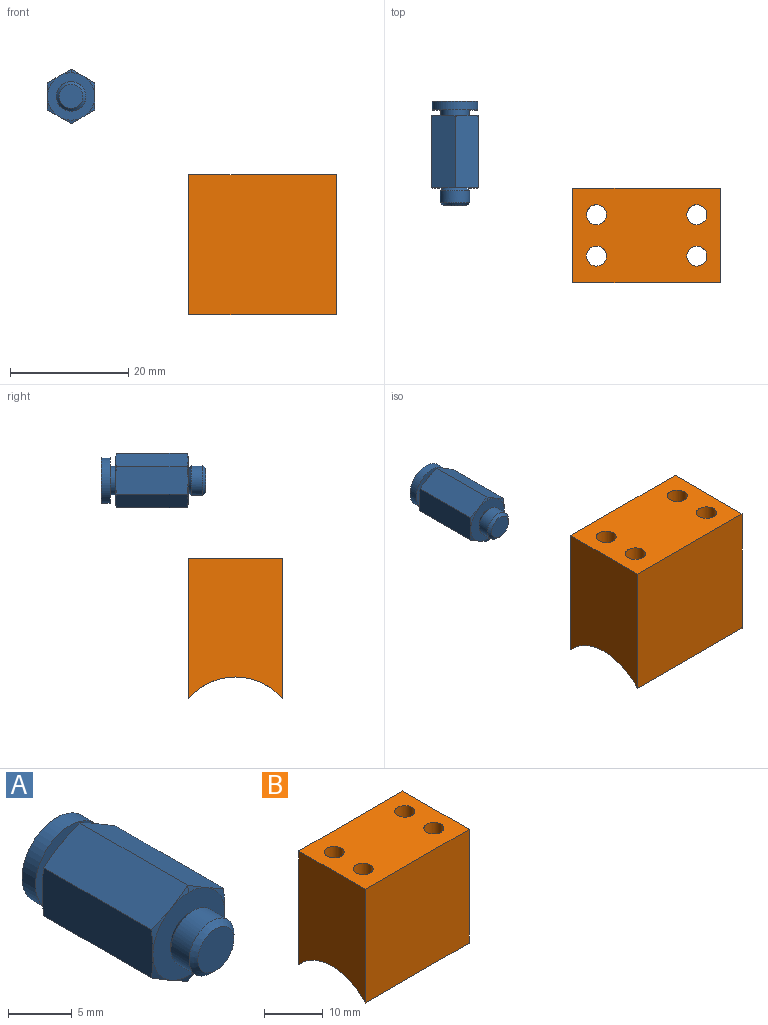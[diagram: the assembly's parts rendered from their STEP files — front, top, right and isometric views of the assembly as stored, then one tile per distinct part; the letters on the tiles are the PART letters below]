
ASSEMBLY  parts=2 mates=1
PART A: 32 faces, bbox 9.6x18x9.6 mm
  f0: plane 4x4mm, normal (0,1,0), area 12.6mm2, adj f1
  f1: cylinder r=2mm len=13.3mm, axis (0,-1,0), area 167.1mm2, adj f0,f2
  f2: plane 7.7x7.7mm, normal (0,1,0), area 34mm2, adj f1,f3
  f3: cylinder r=3.85mm len=7.7mm, axis (0,-1,0), area 36.3mm2, adj f2,f5
  f4: plane 4.02x4.02mm, normal (0,-1,0), area 12.7mm2, adj f6
  f5: plane 7.7x7.7mm, normal (0,-1,0), area 28.5mm2, adj f3,f10
  f6: cone r=0mm half-angle=45deg, axis (0,1,0), area 9.8mm2, adj f4,f12
  f7: cone r=0mm half-angle=75deg, axis (0,-1,0), area 1.4mm2, adj f11,f15,f17
  f8: cone r=0mm half-angle=75deg, axis (0,-1,0), area 0.7mm2, adj f9,f11,f17
  f9: cone r=0mm half-angle=75deg, axis (0,-1,0), area 0.7mm2, adj f8,f13,f17
  f10: cylinder r=2.4mm len=4.8mm, axis (0,-1,0), area 13.6mm2, adj f5,f17
  f11: plane 12.64x4.34mm, normal (0.5,0,-0.87), area 56.3mm2, adj f7,f8,f13,f15,f18,f21
  f12: cylinder r=2.5mm len=5mm, axis (0,-1,0), area 31.7mm2, adj f6,f22
  f13: plane 12.64x4.34mm, normal (-0.5,0,-0.87), area 56.3mm2, adj f9,f11,f14,f20,f21,f23
  f14: cone r=0mm half-angle=75deg, axis (0,-1,0), area 1.4mm2, adj f13,f17,f23
  f15: plane 12.64x4.96mm, normal (1,0,0), area 56.3mm2, adj f7,f11,f16,f18,f19,f25
  f16: cone r=0mm half-angle=75deg, axis (0,-1,0), area 1.4mm2, adj f15,f17,f25
  f17: plane 8x8mm, normal (0,1,0), area 32.2mm2, adj f7,f8,f9,f10,f14,f16,f26,f27
  f18: cone r=0mm half-angle=75deg, axis (0,1,0), area 1.4mm2, adj f11,f15,f28
  f19: cone r=0mm half-angle=75deg, axis (0,1,0), area 1.4mm2, adj f15,f25,f28
  f20: cone r=0mm half-angle=75deg, axis (0,1,0), area 1.4mm2, adj f13,f23,f28
  f21: cone r=0mm half-angle=75deg, axis (0,1,0), area 1.4mm2, adj f11,f13,f28
  f22: cone r=0mm half-angle=45deg, axis (0,-1,0), area 9.8mm2, adj f12,f28
  f23: plane 12.64x4.96mm, normal (-1,0,0), area 56.3mm2, adj f13,f14,f20,f24,f27,f30
  f24: cone r=0mm half-angle=75deg, axis (0,1,0), area 1.4mm2, adj f23,f28,f30
  f25: plane 12.64x4.34mm, normal (0.5,0,0.87), area 56.3mm2, adj f15,f16,f19,f26,f29,f30
  f26: cone r=0mm half-angle=75deg, axis (0,-1,0), area 1.4mm2, adj f17,f25,f30
  f27: cone r=0mm half-angle=75deg, axis (0,-1,0), area 1.4mm2, adj f17,f23,f30
  f28: plane 8x8mm, normal (0,-1,0), area 37.6mm2, adj f18,f19,f20,f21,f22,f24,f29,f31
  f29: cone r=0mm half-angle=75deg, axis (0,1,0), area 0.7mm2, adj f25,f28,f31
  f30: plane 12.64x4.34mm, normal (-0.5,0,0.87), area 56.3mm2, adj f23,f24,f25,f26,f27,f31
  f31: cone r=0mm half-angle=75deg, axis (0,1,0), area 0.7mm2, adj f28,f29,f30
PART B: 25 faces, bbox 25x16x23.7 mm
  f0: plane 25x23.7mm, normal (0,1,0), area 578.6mm2, adj f2,f3,f4,f17,f19
  f1: plane 25x23.7mm, normal (0,-1,0), area 592.5mm2, adj f2,f3,f4,f17
  f2: plane 23.7x16mm, normal (1,0,0), area 338.1mm2, adj f0,f1,f4,f17
  f3: plane 23.7x16mm, normal (-1,0,0), area 338.1mm2, adj f0,f1,f4,f17
  f4: plane 25x16mm, normal (0,0,1), area 363.7mm2, adj f0,f1,f2,f3,f5,f8,f11,f14
  f5: cylinder r=1.7mm len=15mm, axis (0,0,-1), area 160.2mm2, adj f4,f6
  f6: plane 6.5x6.5mm, normal (0,0,-1), area 24.1mm2, adj f5,f7
  f7: cylinder r=3.25mm len=7.46mm, axis (0,0,-1), area 120.7mm2, adj f6,f17
  f8: cylinder r=1.7mm len=15mm, axis (0,0,-1), area 160.2mm2, adj f4,f9
  f9: plane 6.5x6.5mm, normal (0,0,-1), area 24.1mm2, adj f8,f10
  f10: cylinder r=3.25mm len=7.46mm, axis (0,0,-1), area 120.7mm2, adj f9,f17
  f11: cylinder r=1.7mm len=15mm, axis (0,0,-1), area 160.2mm2, adj f4,f12
  f12: plane 6.5x6.5mm, normal (0,0,-1), area 24.1mm2, adj f11,f13
  f13: cylinder r=3.25mm len=7.46mm, axis (0,0,-1), area 120.7mm2, adj f12,f17
  f14: cylinder r=1.7mm len=15mm, axis (0,0,-1), area 160.2mm2, adj f4,f15
  f15: plane 6.5x6.5mm, normal (0,0,-1), area 24.1mm2, adj f14,f16
  f16: cylinder r=3.25mm len=7.46mm, axis (0,0,-1), area 120.7mm2, adj f15,f17
  f17: cylinder r=10.5mm len=25mm, axis (1,0,0), area 301.1mm2, adj f0,f1,f2,f3,f7,f10,f13,f16
  f18: cone r=0mm half-angle=59deg, axis (0,1,0), area 6.9mm2, adj f19,f20,f24
  f19: cylinder r=2.1mm len=4.2mm, axis (0,1,0), area 50.2mm2, adj f0,f18,f24
  f20: cylinder r=1.5mm len=9.64mm, axis (0,1,0), area 84mm2, adj f18,f21,f22,f23,f24
  f21: plane 3x3mm, normal (0,1,0), area 7.1mm2, adj f20
  f22: cylinder r=1mm len=4.93mm, axis (0,0,-1), area 29.6mm2, adj f17,f20
  f23: cylinder r=1mm len=6.44mm, axis (0,0,-1), area 36mm2, adj f17,f20
  f24: cylinder r=1mm len=6.15mm, axis (0,0,-1), area 32.8mm2, adj f17,f18,f19,f20
PLACE A t=(-43.02,4.72,23.13)mm
PLACE B t=(-10.6,-3.28,9.87)mm
MATE planar A.f28 <-> B.f0  axis (0,-1,0) through (-39.02,4.72,23.13)mm
